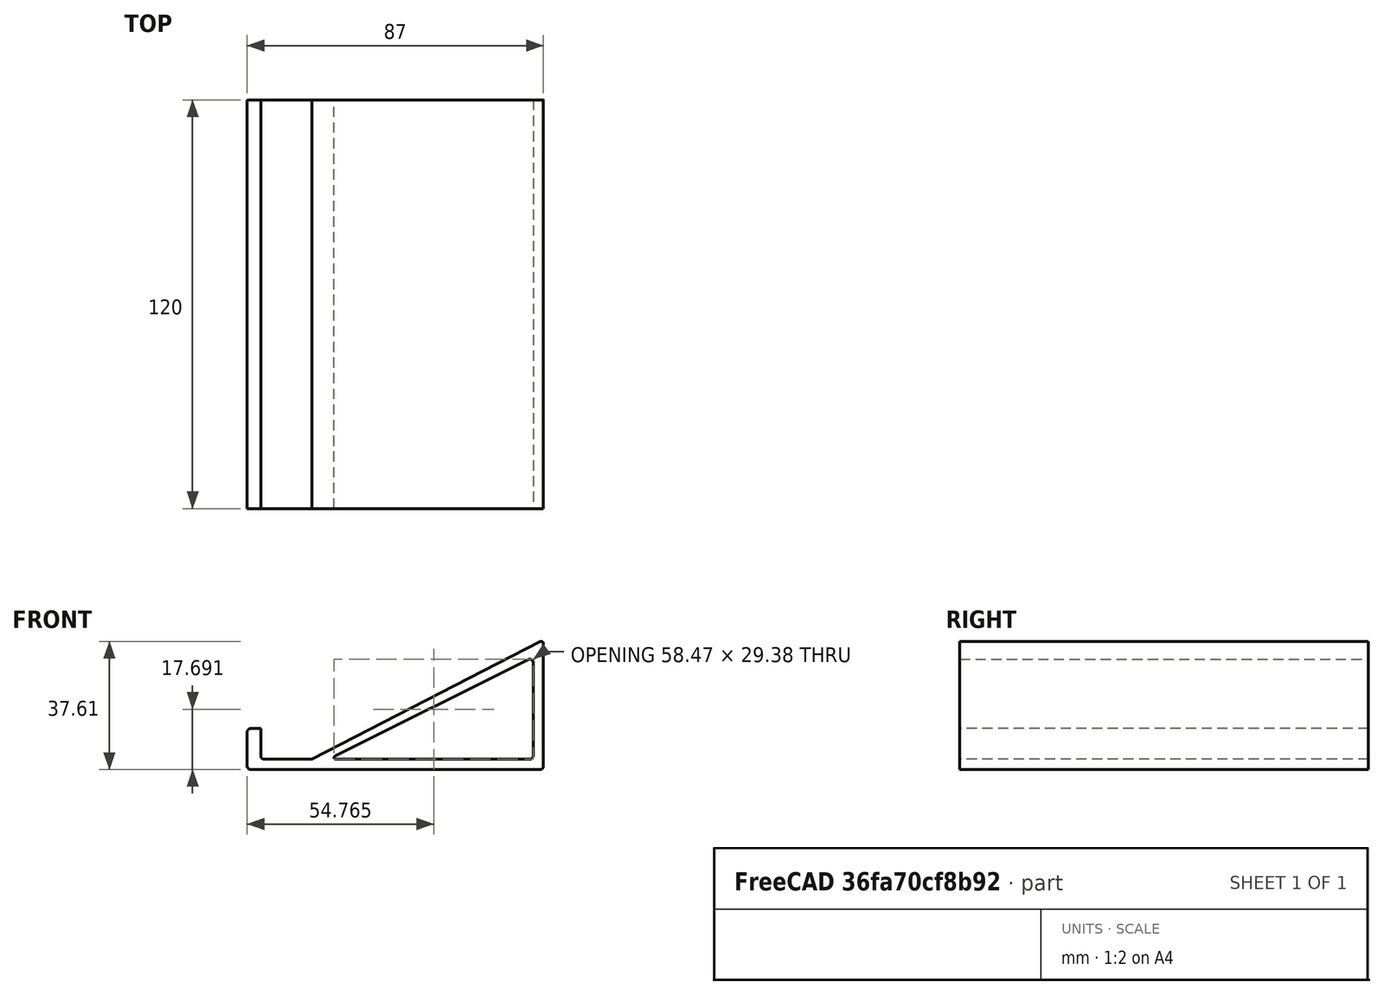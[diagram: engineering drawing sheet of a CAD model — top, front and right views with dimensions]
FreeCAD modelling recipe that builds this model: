
FCSTD DOCUMENT  (FreeCAD 1.0R39109 (Git))
Label: game_smartphone_stand
License: All rights reserved
LicenseURL: https://en.wikipedia.org/wiki/All_rights_reserved
objects: Sketcher::SketchObject×1, PartDesign::Pad×1, PartDesign::Body×1
note: 6 computed .brp shape members not serialized (recipe doc carries the construction recipe); baked Part::Feature solids carry a one-line shape summary decoded from their .brp

FEATURE [Sketcher::SketchObject] Sketch
  ArcFitTolerance = 1e-06
  AttachmentSupport = -> [XZ_Plane]
  FullyConstrained = true
  MakeInternals = false
  MapMode = 5
  Placement = pos=(0,0,0) rot=(1,0,0;1.5708rad)
  sketch-geometry (26):
    g0: LineSegment StartX=2 StartY=0 StartZ=0 EndX=59 EndY=0 EndZ=0
    g1: LineSegment StartX=60 StartY=1 StartZ=0 EndX=60 EndY=28.382 EndZ=0
    g2: LineSegment StartX=58.5528 StartY=29.2764 StartZ=0 EndX=1.78885 EndY=0.894427 EndZ=0
    g3: LineSegment StartX=63 StartY=34 StartZ=0 EndX=63 EndY=-2 EndZ=0
    g4: LineSegment StartX=62.1109 StartY=34.5424 StartZ=0 EndX=-5 EndY=1.1e-15 EndZ=0
    g5: LineSegment StartX=-19 StartY=0 StartZ=0 EndX=-5 EndY=1.1e-15 EndZ=0
    g6: LineSegment StartX=-20 StartY=1 StartZ=0 EndX=-20 EndY=9 EndZ=0
    g7: LineSegment StartX=-20 StartY=9 StartZ=0 EndX=-23 EndY=9 EndZ=0
    g8: LineSegment StartX=-24 StartY=8 StartZ=0 EndX=-24 EndY=-2 EndZ=0
    g9: LineSegment StartX=-23 StartY=-3 StartZ=0 EndX=62 EndY=-3 EndZ=0
    g10: ArcOfCircle CenterX=-23 CenterY=8 CenterZ=0 NormalX=0 NormalY=0 NormalZ=1 AngleXU=0 Radius=1 StartAngle=1.5708 EndAngle=3.14159
    g11: GeomPoint [constr] X=-24 Y=9 Z=0
    g12: ArcOfCircle CenterX=-23 CenterY=-2 CenterZ=0 NormalX=0 NormalY=0 NormalZ=1 AngleXU=0 Radius=1 StartAngle=3.14159 EndAngle=4.71239
    g13: GeomPoint [constr] X=-24 Y=-3 Z=0
    g14: ArcOfCircle CenterX=62 CenterY=-2 CenterZ=0 NormalX=0 NormalY=0 NormalZ=1 AngleXU=0 Radius=1 StartAngle=4.71239 EndAngle=6.28319
    g15: GeomPoint [constr] X=63 Y=-3 Z=0
    g16: ArcOfCircle CenterX=62.39 CenterY=34 CenterZ=0 NormalX=0 NormalY=0 NormalZ=1 AngleXU=0 Radius=0.609982 StartAngle=-2.7e-15 EndAngle=2.04614
    g17: GeomPoint [constr] X=63 Y=35 Z=0
    g18: ArcOfCircle CenterX=59 CenterY=28.382 CenterZ=0 NormalX=0 NormalY=0 NormalZ=1 AngleXU=0 Radius=1 StartAngle=1.5e-15 EndAngle=2.03444
    g19: GeomPoint [constr] X=60 Y=30 Z=0
    g20: ArcOfCircle CenterX=59 CenterY=1 CenterZ=0 NormalX=0 NormalY=0 NormalZ=1 AngleXU=0 Radius=1 StartAngle=4.71239 EndAngle=6.28319
    g21: GeomPoint [constr] X=60 Y=0 Z=0
    g22: ArcOfCircle CenterX=2 CenterY=0.472136 CenterZ=0 NormalX=0 NormalY=0 NormalZ=1 AngleXU=0 Radius=0.472136 StartAngle=2.03444 EndAngle=4.71239
    g23: GeomPoint [constr] X=0 Y=0 Z=0
    g24: ArcOfCircle CenterX=-19 CenterY=1 CenterZ=0 NormalX=0 NormalY=0 NormalZ=1 AngleXU=0 Radius=1 StartAngle=3.14159 EndAngle=4.71239
    g25: GeomPoint [constr] X=-20 Y=0 Z=0
  constraints (61):
    c: Coincident(g23,g-1)
    c: PointOnObject(g21,g-1)
    c: DistanceX(g23,g21) = 60
    c: Vertical(g1)
    c: DistanceY(g21,g19) = 30
    c: Vertical(g3)
    c: PointOnObject(g4,g-1)
    c: PointOnObject(g25,g-1)
    c: Coincident(g5,g4)
    c: Coincident(g7,g6)
    c: Vertical(g8)
    c: Horizontal(g9)
    c: Horizontal(g7)
    c: DistanceY(g19,g17) = 5
    c: DistanceX(g4,g23) = 5
    c: DistanceX(g19,g17) = 3
    c: DistanceY(g15,g21) = 3
    c: DistanceX(g25,g5) = 15
    c: Vertical(g6)
    c: DistanceX(g11,g7) = 4
    c: DistanceY(g25,g6) = 9
    c: PointOnObject(g11,g7)
    c: PointOnObject(g11,g8)
    c: Tangent(g7,g10) = -1.5708
    c: Tangent(g8,g10) = -1.5708
    c: PointOnObject(g13,g8)
    c: PointOnObject(g13,g9)
    c: Tangent(g8,g12) = -1.5708
    c: Tangent(g9,g12) = -1.5708
    c: PointOnObject(g15,g3)
    c: PointOnObject(g15,g9)
    c: Tangent(g3,g14) = 1.5708
    c: Tangent(g9,g14) = -1.5708
    c: PointOnObject(g17,g3)
    c: PointOnObject(g17,g4)
    c: Tangent(g3,g16) = 1.5708
    c: Tangent(g4,g16) = -1.5708
    c: DistanceY(g10,g7) = 1
    c: DistanceY(g9,g12) = 1
    c: DistanceY(g15,g3) = 1
    c: DistanceY(g3,g17) = 1
    c: PointOnObject(g19,g1)
    c: PointOnObject(g19,g2)
    c: Tangent(g1,g18) = -1.5708
    c: Tangent(g2,g18) = -1.5708
    c: PointOnObject(g21,g0)
    c: PointOnObject(g21,g1)
    c: Tangent(g0,g20) = -1.5708
    c: Tangent(g1,g20) = -1.5708
    c: DistanceX(g0,g21) = 1
    c: DistanceX(g18,g1) = 1
    c: PointOnObject(g23,g2)
    c: PointOnObject(g23,g0)
    c: Tangent(g2,g22) = -1.5708
    c: Tangent(g0,g22) = -1.5708
    c: DistanceX(g23,g0) = 2
    c: PointOnObject(g25,g5)
    c: PointOnObject(g25,g6)
    c: Tangent(g5,g24) = -1.5708
    c: Tangent(g6,g24) = 1.5708
    c: DistanceX(g6,g24) = 1
FEATURE [PartDesign::Pad] Pad
  Direction = (0,-1,2e-16)
  Length = 120
  Length2 = 10
  Placement = pos=(0,0,0) rot=(1,0,0;1.5708rad)
  Profile = -> Sketch
  ReferenceAxis = -> Sketch [N_Axis]
  Refine = true
  Suppressed = false
  Type = 0
FEATURE [PartDesign::Body] Body
  AllowCompound = false
  Group = -> [Sketch,Pad]
  Origin = -> Origin
  Tip = -> Pad
